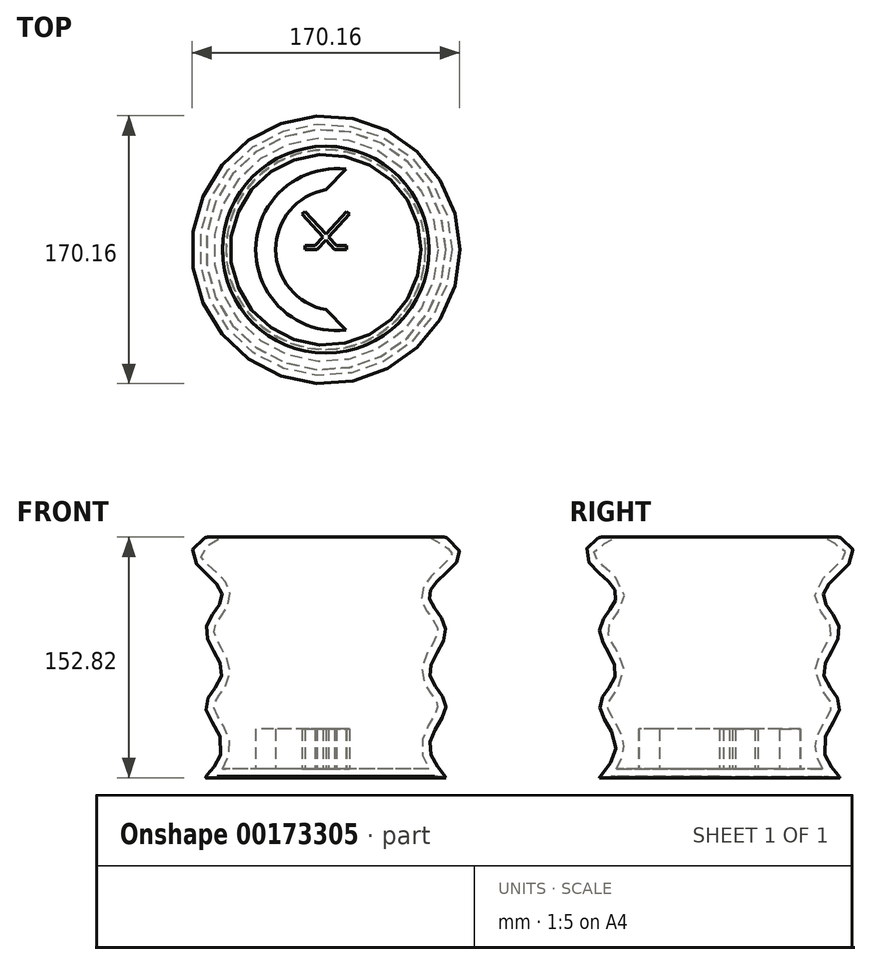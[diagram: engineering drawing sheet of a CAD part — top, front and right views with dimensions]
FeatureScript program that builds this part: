
annotation { "Feature Type Name" : "Feature", "Feature Type Description" : "" }
export const myFeature = defineFeature(function(context is Context, id is Id, definition is map)
    precondition{}
    {
        {
            var Q0;
            Q0=qCreatedBy(makeId("Front.planeOp"),FACE);
            var sketch = newSketch(context, id + "F0", { "sketchPlane" : qUnion([Q0])});
            skLineSegment(sketch, "E0", {"start": v(0, 85.89) * mm, "end": v(0, -66.51) * mm});
            skLineSegment(sketch, "E1", {"start": v(0, -66.51) * mm, "end": v(63.5, -66.51) * mm});
            skLineSegment(sketch, "E2", {"start": v(0, 85.89) * mm, "end": v(76.2, 85.89) * mm});
            skFitSpline(sketch, "E3", {"points": [v(76.2, 85.89) * mm, v(76.2, 62.88) * mm, v(65.84, 46.9) * mm, v(76.2, 26.53) * mm, v(65.84, 0) * mm, v(76.2, -21.03) * mm, v(65.84, -47.6) * mm, v(76.2, -66.51) * mm, v(63.5, -66.51) * mm], "startDerivative": vector(372.56, -206.12) * mm, "endDerivative": vector(-325.69, -40.42) * mm});
            skSolve(sketch);
        }
        {
            var Q0;
            Q0=makeQuery(id+"F0.imprint","IMPRINT",FACE,{"disambiguationData":[TD([[makeQuery(id+"F0.imprint","IMPRINT",EDGE,{"derivedFrom":sQuery(id+"F0.wireOp",EDGE,"E0")}),1.0]])]});
            var Q1;
            Q1=sQuery(id+"F0.wireOp",EDGE,"E0");
            revolve(context, id + "F1", {"entities" : qUnion([Q0]), "axis" : qUnion([Q1]), "revolveType" : RevolveType.FULL});
        }
        {
            var Q0;
            Q0=makeQuery(id+"F1.opRevolve","SWEPT_FACE",FACE,{"disambiguationData":[OSD([sQuery(id+"F0.wireOp",EDGE,"E2")])]});
            shell(context, id + "F2", {"entities" : qUnion([Q0]), "thickness" : 5.08 * mm});
        }
        {
            var Q0;
            Q0=makeQuery(id+"F1.opRevolve","SWEPT_EDGE",EDGE,{"disambiguationData":[OSD([sQuery(id+"F0.wireOp",EDGE,"E2"),sQuery(id+"F0.wireOp",EDGE,"5fd99345-142e-4c7f-bdb4-03190a5b153b")])]});
            fillet(context, id + "F3", {"entities" : qUnion([Q0]), "radius" : 5.08 * mm, "tangentPropagation" : true, "allowEdgeOverflow" : false});
        }
        {
            var Q0;
            Q0=makeQuery(id+"F2.opShell","OFFSET_FACE",FACE,{"disambiguationData":[OSD([sQuery(id+"F0.wireOp",EDGE,"E1")])]});
            var sketch = newSketch(context, id + "F4", { "sketchPlane" : qUnion([Q0])});
            skLineSegment(sketch, "E4", {"start": v(-13.18, 0) * mm, "end": v(-5.56, 0) * mm});
            skLineSegment(sketch, "E5", {"start": v(-13.18, 0) * mm, "end": v(-13.18, 2.54) * mm});
            skLineSegment(sketch, "E6", {"start": v(-5.56, 0) * mm, "end": v(14.96, 22.54) * mm});
            skLineSegment(sketch, "E7", {"start": v(14.96, 22.54) * mm, "end": v(13.08, 24.25) * mm});
            skLineSegment(sketch, "E8", {"start": v(13.08, 24.25) * mm, "end": v(-6.68, 2.54) * mm});
            skLineSegment(sketch, "E9", {"start": v(-13.18, 2.54) * mm, "end": v(-6.68, 2.54) * mm});
            skLineSegment(sketch, "E10.MirrorCS", {"start": v(13.18, 2.54) * mm, "end": v(6.68, 2.54) * mm});
            skLineSegment(sketch, "E11.MirrorCS", {"start": v(13.18, 0) * mm, "end": v(13.18, 2.54) * mm});
            skLineSegment(sketch, "E12.MirrorCS", {"start": v(13.18, 0) * mm, "end": v(5.56, 0) * mm});
            skLineSegment(sketch, "E13.MirrorCS", {"start": v(5.56, 0) * mm, "end": v(-14.96, 22.54) * mm});
            skLineSegment(sketch, "E14.MirrorCS", {"start": v(-13.08, 24.25) * mm, "end": v(6.68, 2.54) * mm});
            skLineSegment(sketch, "E15.MirrorCS", {"start": v(-14.96, 22.54) * mm, "end": v(-13.08, 24.25) * mm});
            skSolve(sketch);
        }
        {
            var Q0;
            {var subQ5=sQuery(id+"F4.wireOp",EDGE,"E15.MirrorCS");Q0=makeQuery(id+"F4.imprint","IMPRINT",FACE,{"disambiguationData":[TD([[makeQuery(id+"F4.imprint","IMPRINT",EDGE,{"derivedFrom":subQ5}),-1.0]])]});}
            var Q1;
            {var subQ0=sQuery(id+"F4.wireOp",EDGE,"E7");Q1=makeQuery(id+"F4.imprint","IMPRINT",FACE,{"disambiguationData":[TD([[makeQuery(id+"F4.imprint","IMPRINT",EDGE,{"derivedFrom":subQ0}),1.0]])]});}
            var Q2;
            {var subQ0=sQuery(id+"F4.wireOp",EDGE,"E13.MirrorCS");var subQ1=sQuery(id+"F4.wireOp",EDGE,"E6");var subQ2=makeQuery(id+"F4.imprint","INTERSECT",VERTEX,{"derivedFrom":[subQ1,subQ0]});Q2=makeQuery(id+"F4.imprint","IMPRINT",FACE,{"disambiguationData":[TD([[makeQuery(id+"F4.imprint","IMPRINT",EDGE,{"disambiguationData":[TD([[subQ2,-1.0]])],"derivedFrom":subQ1}),1.0]])]});}
            var Q3;
            {var subQ5=sQuery(id+"F4.wireOp",EDGE,"E4");Q3=makeQuery(id+"F4.imprint","IMPRINT",FACE,{"disambiguationData":[TD([[makeQuery(id+"F4.imprint","IMPRINT",EDGE,{"derivedFrom":subQ5}),1.0]])]});}
            var Q4;
            {var subQ1=sQuery(id+"F4.wireOp",EDGE,"E10.MirrorCS");Q4=makeQuery(id+"F4.imprint","IMPRINT",FACE,{"disambiguationData":[TD([[makeQuery(id+"F4.imprint","IMPRINT",EDGE,{"derivedFrom":subQ1}),1.0]])]});}
            extrude(context, id + "F5", {"entities" : qUnion([Q0, Q1, Q2, Q3, Q4]), "operationType" : NewBodyOperationType.ADD, "depth" : 25.4 * mm});
        }
        {
            var Q0;
            Q0=makeQuery(id+"F2.opShell","OFFSET_FACE",FACE,{"disambiguationData":[OSD([sQuery(id+"F0.wireOp",EDGE,"E1")])]});
            var sketch = newSketch(context, id + "F6", { "sketchPlane" : qUnion([Q0])});
            skLineSegment(sketch, "E16", {"start": v(0, 0) * mm, "end": v(0, 38.1) * mm});
            skLineSegment(sketch, "E17", {"start": v(0, 0) * mm, "end": v(0, -38.1) * mm});
            skArc(sketch, "E18", {"start": v(0, 38.1) * mm, "mid": v(-31.8, 0) * mm, "end": v(0, -38.1) * mm});
            skArc(sketch, "E19.0", {"start": v(12.7, 51.1) * mm, "mid": v(-44.5, 0) * mm, "end": v(12.7, -51.1) * mm});
            skLineSegment(sketch, "E20", {"start": v(0, 38.1) * mm, "end": v(12.7, 51.1) * mm});
            skLineSegment(sketch, "E21", {"start": v(0, -38.1) * mm, "end": v(12.7, -51.1) * mm});
            skSolve(sketch);
        }
        {
            var Q0;
            Q0=makeQuery(id+"F6.imprint","IMPRINT",FACE,{"disambiguationData":[TD([[makeQuery(id+"F6.imprint","IMPRINT",EDGE,{"derivedFrom":sQuery(id+"F6.wireOp",EDGE,"E18")}),-1.0]])]});
            extrude(context, id + "F7", {"entities" : qUnion([Q0]), "operationType" : NewBodyOperationType.ADD, "depth" : 25.4 * mm});
        }
    });
